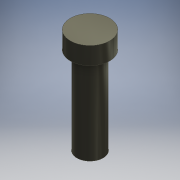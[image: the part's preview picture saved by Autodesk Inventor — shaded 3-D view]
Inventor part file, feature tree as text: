
AUTODESK INVENTOR PART (.ipt)
format: ipt  version: 2016 (Build 200138000, 138)  size: 97,792 bytes
history: native  units: mm
features: extrude x2, other x1, sketch x1
ambient origin geometry x8: Origin, YZ Plane, XZ Plane, XY Plane, X Axis, Y Axis, Z Axis, Center Point
bodies: Body1 (feature_tree)
feature tree (4):
  other  "ソリッド1"
  sketch  "スケッチ1"
  extrude  "押し出し1"  Depth=4.5mm
  extrude  "押し出し2"  Depth=3.0mm
